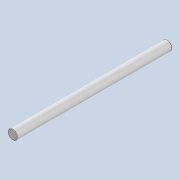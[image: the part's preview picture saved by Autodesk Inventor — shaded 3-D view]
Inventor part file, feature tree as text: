
AUTODESK INVENTOR PART (.ipt)
format: ipt  version: 2020 (Build 240168000, 168)  size: 91,136 bytes
history: native  units: mm
features: extrude x1, chamfer x1, sketch x1
ambient origin geometry x8: Origin, YZ Plane, XZ Plane, XY Plane, X Axis, Y Axis, Z Axis, Center Point
bodies: Solid1 (feature_tree)
feature tree (3):
  extrude  "Extrusion1"  Depth=166.0mm TaperAngle=0.0deg
  chamfer  "Chamfer1"  Distance=0.5mm Angle=45.0deg
  sketch  "Sketch1"  dims[d0=10.0mm d1=166.0mm d2=0.0mm d3=0.5mm d4=2.0mm d5=45.0deg]
